# Revit family: Bernhardt-Design_Seating_Chapelle_1-Seat_Full-Wall
name_source: partatom
category: Furniture
revit_build: Autodesk Revit 2016 (Build: 20150714_1515(x64)
units: mm (PartAtom-declared; Revit-internal decimal feet)

## family parameters
Always vertical = Yes
Cut with Voids When Loaded = No
OmniClass Number = 23.40.70.14.64
OmniClass Title = Retail and Commercial Furnishings
Room Calculation Point = No
Shared = No
Work Plane-Based = No

## types (1)
- 2 Seat Full Wall
    Bernhardt Fabric = <By Category>
    Description = Seating
    Height = 3' - 11 3/8"
    Length = 65' - 9"
    Manufacturer = Bernhardt Design
    Mid Wall = 4' - 1 13/16"
    Model = Chapelle
    Product Documentation Link = http://www.bernhardtdesign.com
    Product Name = Chapelle
    Product Page URL = http://www.bernhardtdesign.com
    URL = http://bernhardtdesign.com
    Width = 2' - 4 1/4"

## geometry (parser evidence)
native form markers: Blend x2, Sweep x4
no freeform markers — native parametric forms only
